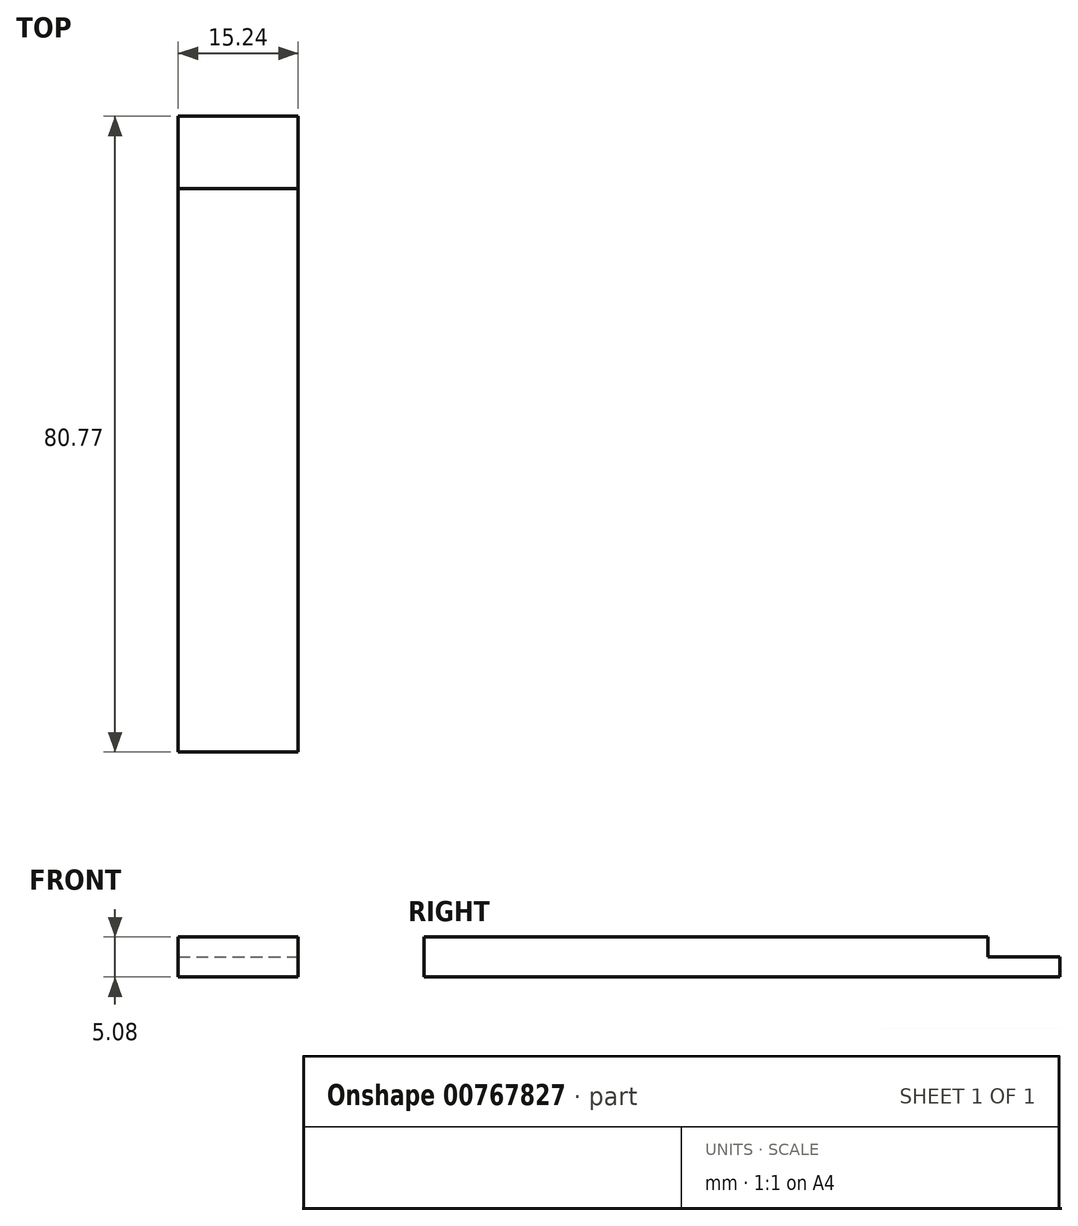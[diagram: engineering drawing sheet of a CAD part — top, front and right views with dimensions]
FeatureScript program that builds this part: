
annotation { "Feature Type Name" : "Feature", "Feature Type Description" : "" }
export const myFeature = defineFeature(function(context is Context, id is Id, definition is map)
    precondition{}
    {
        {
            var Q0;
            Q0=qCreatedBy(makeId("Front.planeOp"),FACE);
            var sketch = newSketch(context, id + "F0", { "sketchPlane" : qUnion([Q0])});
            skLineSegment(sketch, "E0.bottom", {"start": v(-15.24, 5.08) * mm, "end": v(0, 5.08) * mm});
            skLineSegment(sketch, "E0.top", {"start": v(-15.24, 0) * mm, "end": v(0, 0) * mm});
            skLineSegment(sketch, "E0.left", {"start": v(-15.24, 5.08) * mm, "end": v(-15.24, 0) * mm});
            skLineSegment(sketch, "E0.right", {"start": v(0, 5.08) * mm, "end": v(0, 0) * mm});
            skSolve(sketch);
        }
        {
            var Q0;
            Q0 = qSketchRegion(id + "F0", true);
            extrude(context, id + "F1", {"entities" : qUnion([Q0]), "depth" : 80.77 * mm, "offsetDistance" : 25.4 * mm});
        }
        {
            var Q0;
            Q0=makeQuery(id+"F1.opExtrude","SWEPT_FACE",FACE,{"disambiguationData":[OSD([sQuery(id+"F0.wireOp",EDGE,"E0.bottom")])]});
            var sketch = newSketch(context, id + "F2", { "sketchPlane" : qUnion([Q0])});
            skLineSegment(sketch, "E1.bottom", {"start": v(-15.24, 0) * mm, "end": v(0, 0) * mm});
            skLineSegment(sketch, "E1.top", {"start": v(-15.24, -9.17) * mm, "end": v(0, -9.17) * mm});
            skLineSegment(sketch, "E1.left", {"start": v(-15.24, 0) * mm, "end": v(-15.24, -9.17) * mm});
            skLineSegment(sketch, "E1.right", {"start": v(0, 0) * mm, "end": v(0, -9.17) * mm});
            skSolve(sketch);
        }
        {
            var Q0;
            Q0 = qSketchRegion(id + "F2", true);
            extrude(context, id + "F3", {"entities" : qUnion([Q0]), "operationType" : NewBodyOperationType.REMOVE, "oppositeDirection" : true, "depth" : 2.54 * mm, "offsetDistance" : 25.4 * mm});
        }
    });
